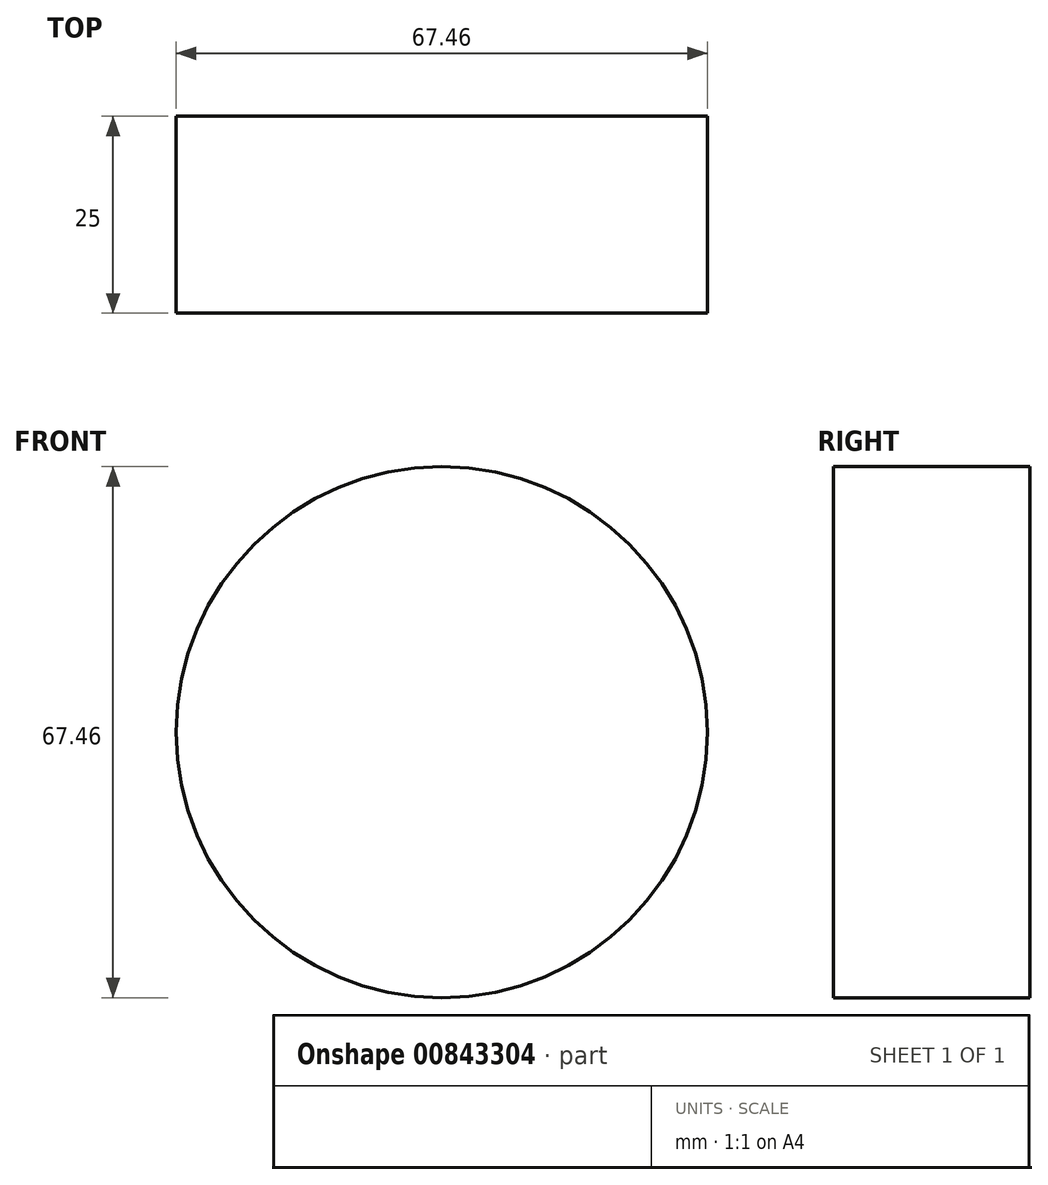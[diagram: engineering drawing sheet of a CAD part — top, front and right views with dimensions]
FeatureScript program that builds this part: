
annotation { "Feature Type Name" : "Feature", "Feature Type Description" : "" }
export const myFeature = defineFeature(function(context is Context, id is Id, definition is map)
    precondition{}
    {
        {
            var Q0;
            Q0=qCreatedBy(makeId("Front.planeOp"),FACE);
            var sketch = newSketch(context, id + "F0", { "sketchPlane" : qUnion([Q0])});
            skCircle(sketch, "E0", {"center": v(-64.38, 10.7) * mm, "radius": 33.73 * mm});
            skSolve(sketch);
        }
        {
            var Q0;
            Q0 = qSketchRegion(id + "F0", true);
            extrude(context, id + "F1", {"entities" : qUnion([Q0]), "depth" : 25 * mm, "offsetDistance" : 25 * mm});
        }
    });
